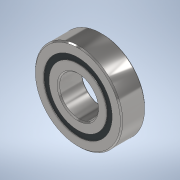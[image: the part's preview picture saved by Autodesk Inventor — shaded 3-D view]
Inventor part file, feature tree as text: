
AUTODESK INVENTOR PART (.ipt)
format: ipt  version: 2020 (Build 240168000, 168)  size: 552,960 bytes
history: native  units: in
note: dims shown in document units (in); Inventor stores cm internally (conversion verified against a paired STEP export)
features: other x9, revolve x5
ambient origin geometry x8: Origin, YZ Plane, XZ Plane, XY Plane, X Axis, Y Axis, Z Axis, Center Point
bodies: Solid1 (feature_tree), Solid2 (feature_tree), Solid3 (feature_tree), Solid4 (feature_tree), Solid5 (feature_tree), Solid6 (feature_tree), Solid7 (feature_tree), Solid8 (feature_tree), Solid9 (feature_tree), Solid10 (feature_tree), Solid11 (feature_tree), Solid12 (feature_tree), Solid13 (feature_tree), Solid14 (feature_tree)
feature tree (14):
  revolve  "Revolve1"  [1 undecoded]
  revolve  "Revolve3"  [1 undecoded]
  revolve  "Revolve4"  [1 undecoded]
  other  "CirPattern1[1]"
  other  "CirPattern1[2]"
  other  "CirPattern1[3]"
  other  "CirPattern1[4]"
  other  "CirPattern1[5]"
  other  "CirPattern1[6]"
  other  "CirPattern1[7]"
  other  "CirPattern1[8]"
  other  "CirPattern1[9]"
  revolve  "Revolve5[1]"  [1 undecoded]
  revolve  "Revolve5[2]"  [1 undecoded]
note: 5 required parameter values undecoded (feature->parameter linkage not recoverable at this tier; creation-order binding heuristic only, values carry confidence <= 0.55)
